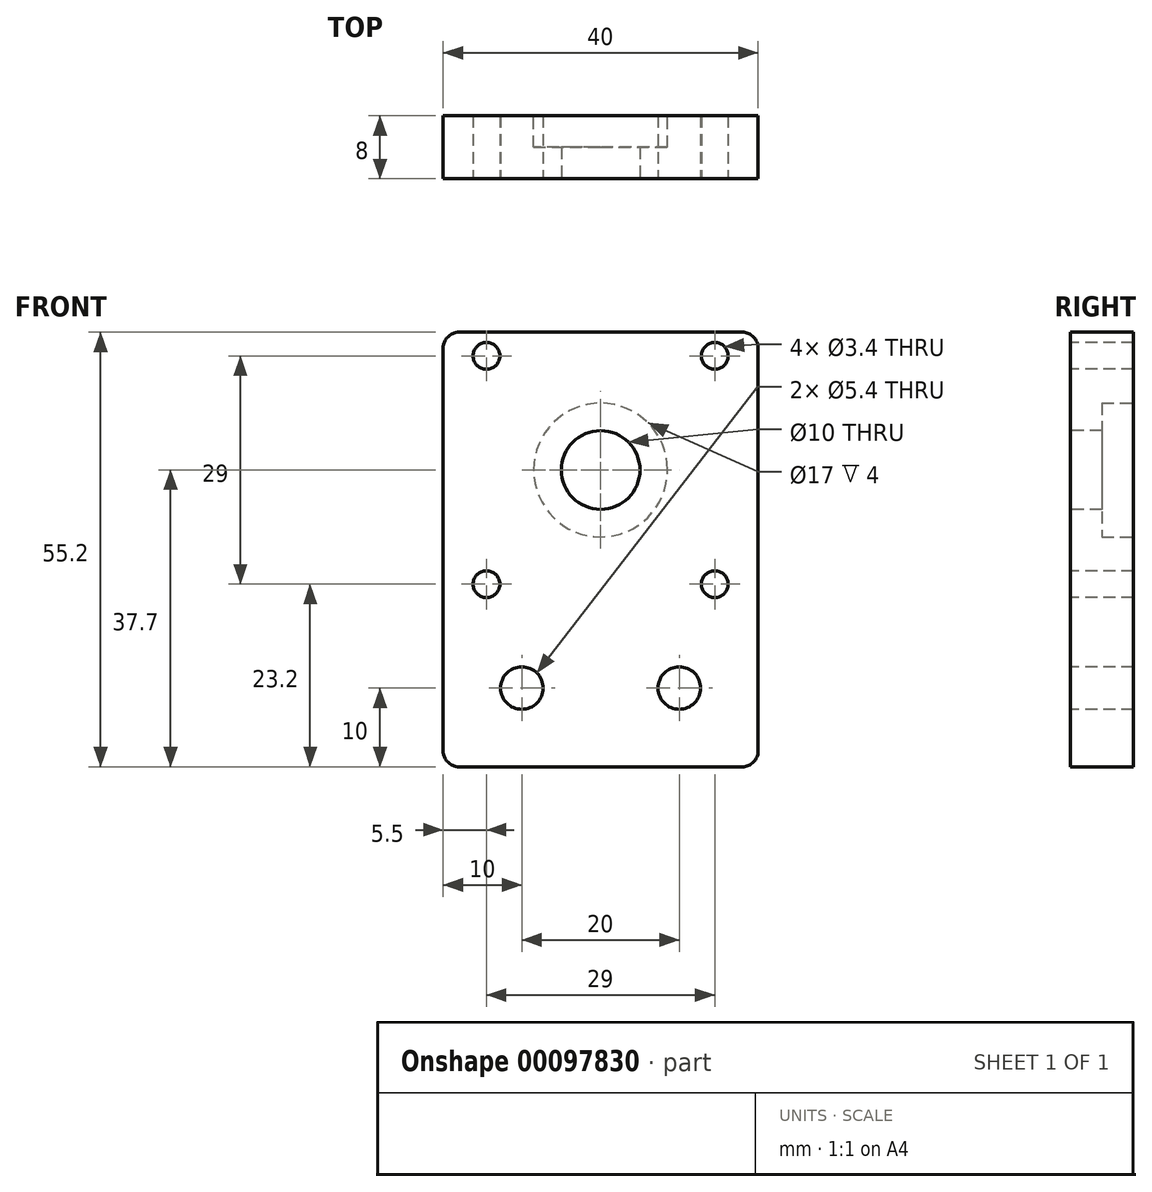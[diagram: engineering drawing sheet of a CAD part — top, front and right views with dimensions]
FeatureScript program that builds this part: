
annotation { "Feature Type Name" : "Feature", "Feature Type Description" : "" }
export const myFeature = defineFeature(function(context is Context, id is Id, definition is map)
    precondition{}
    {
        {
            var Q0;
            Q0=qCreatedBy(makeId("Front.planeOp"),FACE);
            var sketch = newSketch(context, id + "F0", { "sketchPlane" : qUnion([Q0])});
            skLineSegment(sketch, "E0.bottom", {"start": v(20, -17.5) * mm, "end": v(-20, -17.5) * mm, "construction": true});
            skLineSegment(sketch, "E0.top", {"start": v(20, 17.5) * mm, "end": v(-20, 17.5) * mm, "construction": true});
            skLineSegment(sketch, "E0.left", {"start": v(20, -17.5) * mm, "end": v(20, 17.5) * mm, "construction": true});
            skLineSegment(sketch, "E0.right", {"start": v(-20, -17.5) * mm, "end": v(-20, 17.5) * mm, "construction": true});
            skPoint(sketch, "E0.middle", {"position": v(0, 0) * mm});
            skLineSegment(sketch, "E1.bottom", {"start": v(14.5, -14.5) * mm, "end": v(-14.5, -14.5) * mm, "construction": true});
            skLineSegment(sketch, "E1.top", {"start": v(14.5, 14.5) * mm, "end": v(-14.5, 14.5) * mm, "construction": true});
            skLineSegment(sketch, "E1.left", {"start": v(14.5, -14.5) * mm, "end": v(14.5, 14.5) * mm, "construction": true});
            skLineSegment(sketch, "E1.right", {"start": v(-14.5, -14.5) * mm, "end": v(-14.5, 14.5) * mm, "construction": true});
            skCircle(sketch, "E2", {"center": v(-14.5, 14.5) * mm, "radius": 1.7 * mm});
            skCircle(sketch, "E3", {"center": v(14.5, 14.5) * mm, "radius": 1.7 * mm});
            skCircle(sketch, "E4", {"center": v(14.5, -14.5) * mm, "radius": 1.7 * mm});
            skCircle(sketch, "E5", {"center": v(-14.5, -14.5) * mm, "radius": 1.7 * mm});
            skCircle(sketch, "E6", {"center": v(0, 0) * mm, "radius": 4 * mm, "construction": true});
            skCircle(sketch, "E7", {"center": v(0, 0) * mm, "radius": 10 * mm, "construction": true});
            skLineSegment(sketch, "E8", {"start": v(20, -37.7) * mm, "end": v(-20, -37.7) * mm, "construction": true});
            skLineSegment(sketch, "E9", {"start": v(-20, 15.5) * mm, "end": v(-20, -35.7) * mm});
            skLineSegment(sketch, "E10", {"start": v(-18, 17.5) * mm, "end": v(18, 17.5) * mm});
            skLineSegment(sketch, "E11", {"start": v(20, 15.5) * mm, "end": v(20, -35.7) * mm});
            skLineSegment(sketch, "E12", {"start": v(18, -37.7) * mm, "end": v(-18, -37.7) * mm});
            skLineSegment(sketch, "E13", {"start": v(20, -27.7) * mm, "end": v(-20, -27.7) * mm, "construction": true});
            skPoint(sketch, "E14", {"position": v(0, -27.7) * mm});
            skLineSegment(sketch, "E15", {"start": v(0, -27.7) * mm, "end": v(-20, -27.7) * mm, "construction": true});
            skPoint(sketch, "E16", {"position": v(-10, -27.7) * mm});
            skLineSegment(sketch, "E17", {"start": v(0, -27.7) * mm, "end": v(20, -27.7) * mm, "construction": true});
            skPoint(sketch, "E18", {"position": v(10, -27.7) * mm});
            skCircle(sketch, "E19", {"center": v(-10, -27.7) * mm, "radius": 2.7 * mm});
            skCircle(sketch, "E20", {"center": v(10, -27.7) * mm, "radius": 2.7 * mm});
            skPoint(sketch, "E21.visualSharp", {"position": v(-20, 17.5) * mm});
            skArc(sketch, "E21.filletArc", {"start": v(-18, 17.5) * mm, "mid": v(-19.41, 16.91) * mm, "end": v(-20, 15.5) * mm});
            skPoint(sketch, "E22.visualSharp", {"position": v(20, 17.5) * mm});
            skArc(sketch, "E22.filletArc", {"start": v(20, 15.5) * mm, "mid": v(19.41, 16.91) * mm, "end": v(18, 17.5) * mm});
            skPoint(sketch, "E23.visualSharp", {"position": v(20, -37.7) * mm});
            skArc(sketch, "E23.filletArc", {"start": v(18, -37.7) * mm, "mid": v(19.41, -37.11) * mm, "end": v(20, -35.7) * mm});
            skPoint(sketch, "E24.visualSharp", {"position": v(-20, -37.7) * mm});
            skArc(sketch, "E24.filletArc", {"start": v(-20, -35.7) * mm, "mid": v(-19.41, -37.11) * mm, "end": v(-18, -37.7) * mm});
            skCircle(sketch, "E25", {"center": v(0, 0) * mm, "radius": 5 * mm});
            skSolve(sketch);
        }
        {
            var Q0;
            Q0=qSketchRegion(id+"F0",true);
            extrude(context, id + "F1", {"entities" : qUnion([Q0]), "oppositeDirection" : true, "depth" : 8 * mm});
        }
        {
            var Q0;
            Q0=makeQuery(id+"F1.opExtrude","CAP_FACE",FACE,{"disambiguationData":[OSD([sQuery(id+"F0.wireOp",EDGE,"E2"),sQuery(id+"F0.wireOp",EDGE,"E3"),sQuery(id+"F0.wireOp",EDGE,"E4"),sQuery(id+"F0.wireOp",EDGE,"E5"),sQuery(id+"F0.wireOp",EDGE,"E9"),sQuery(id+"F0.wireOp",EDGE,"E10"),sQuery(id+"F0.wireOp",EDGE,"E11"),sQuery(id+"F0.wireOp",EDGE,"E12"),sQuery(id+"F0.wireOp",EDGE,"E19"),sQuery(id+"F0.wireOp",EDGE,"E20"),sQuery(id+"F0.wireOp",EDGE,"E21.filletArc"),sQuery(id+"F0.wireOp",EDGE,"E22.filletArc"),sQuery(id+"F0.wireOp",EDGE,"E23.filletArc"),sQuery(id+"F0.wireOp",EDGE,"E24.filletArc"),sQuery(id+"F0.wireOp",EDGE,"E25")])],"isStart":false});
            var sketch = newSketch(context, id + "F2", { "sketchPlane" : qUnion([Q0])});
            skCircle(sketch, "E26", {"center": v(0, 0) * mm, "radius": 8.5 * mm});
            skSolve(sketch);
        }
        {
            var Q0;
            Q0 = qSketchRegion(id + "F2", true);
            extrude(context, id + "F3", {"entities" : qUnion([Q0]), "operationType" : NewBodyOperationType.REMOVE, "oppositeDirection" : true, "depth" : 4 * mm});
        }
    });
